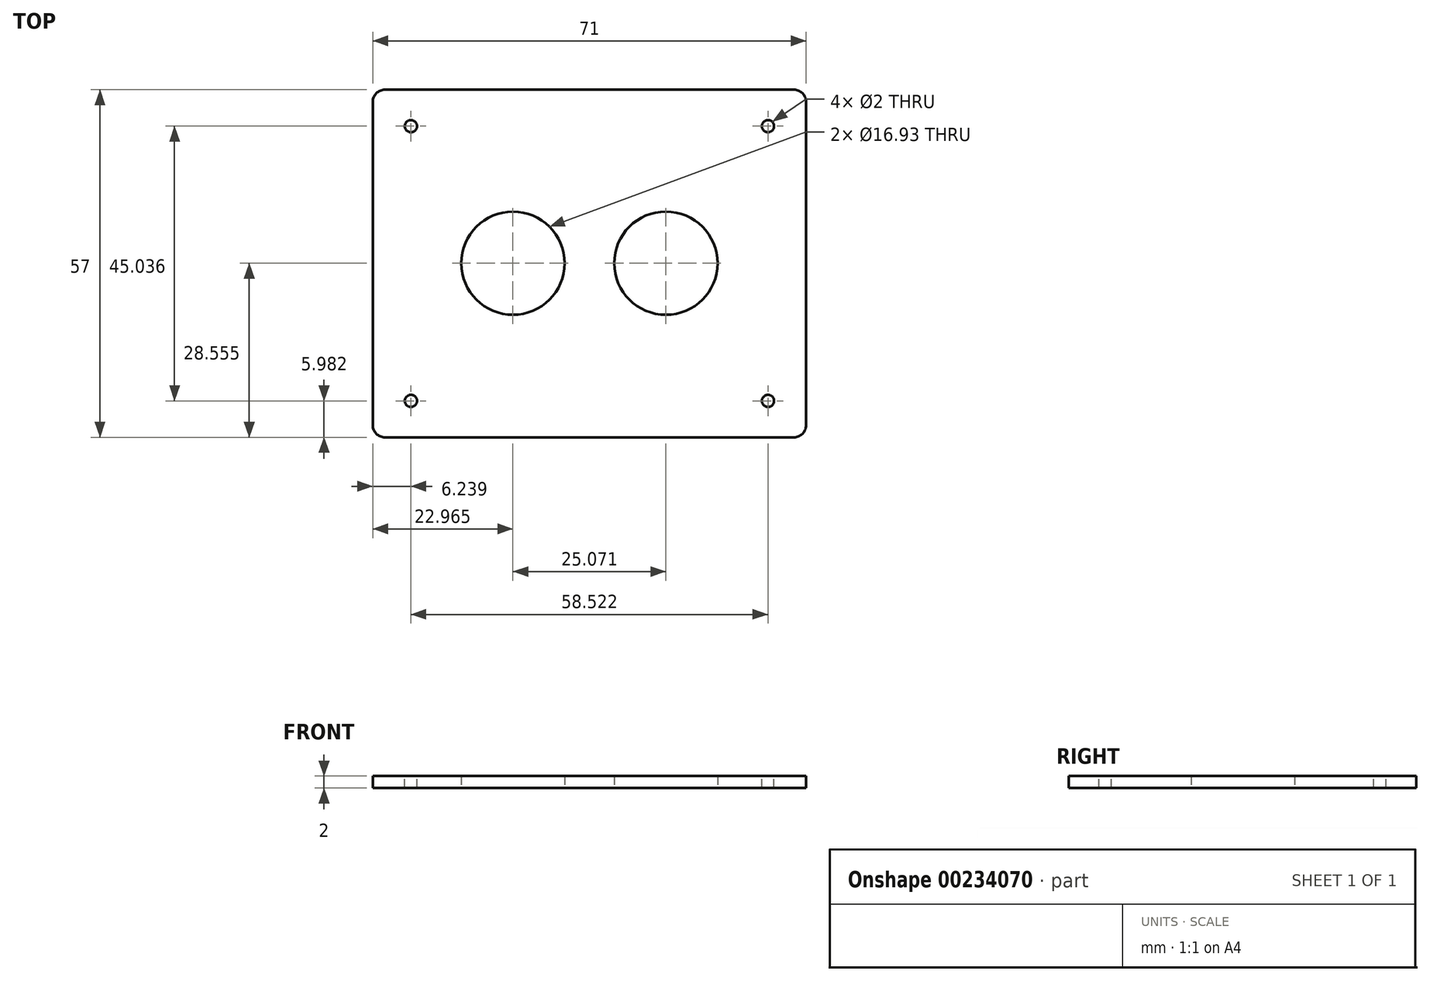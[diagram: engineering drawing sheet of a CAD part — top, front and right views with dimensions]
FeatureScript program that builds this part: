
annotation { "Feature Type Name" : "Feature", "Feature Type Description" : "" }
export const myFeature = defineFeature(function(context is Context, id is Id, definition is map)
    precondition{}
    {
        {
            var Q0;
            Q0=qCreatedBy(makeId("Top.planeOp"),FACE);
            var sketch = newSketch(context, id + "F0", { "sketchPlane" : qUnion([Q0])});
            skLineSegment(sketch, "E0.bottom", {"start": v(21, -8.5) * mm, "end": v(-21, -8.5) * mm, "construction": true});
            skLineSegment(sketch, "E0.top", {"start": v(21, 8.5) * mm, "end": v(-21, 8.5) * mm, "construction": true});
            skLineSegment(sketch, "E0.left", {"start": v(21, -8.5) * mm, "end": v(21, 8.5) * mm, "construction": true});
            skLineSegment(sketch, "E0.right", {"start": v(-21, -8.5) * mm, "end": v(-21, 8.5) * mm, "construction": true});
            skPoint(sketch, "E0.middle", {"position": v(0, 0) * mm});
            skLineSegment(sketch, "E1.bottom", {"start": v(35.5, -28.5) * mm, "end": v(-35.5, -28.5) * mm});
            skLineSegment(sketch, "E1.top", {"start": v(35.5, 28.5) * mm, "end": v(-35.5, 28.5) * mm});
            skLineSegment(sketch, "E1.left", {"start": v(35.5, -28.5) * mm, "end": v(35.5, 28.5) * mm});
            skLineSegment(sketch, "E1.right", {"start": v(-35.5, -28.5) * mm, "end": v(-35.5, 28.5) * mm});
            skPoint(sketch, "E2", {"position": v(-29.77, 22.85) * mm});
            skPoint(sketch, "E3.MirrorP", {"position": v(29.77, 22.85) * mm});
            skPoint(sketch, "E4.MirrorP", {"position": v(-29.77, -22.85) * mm});
            skPoint(sketch, "E5.MirrorP", {"position": v(29.77, -22.85) * mm});
            skCircle(sketch, "E6", {"center": v(-12.54, 0.06) * mm, "radius": 8.46 * mm});
            skPoint(sketch, "E6.first.point", {"position": v(-21, 0) * mm});
            skPoint(sketch, "E6.second.point", {"position": v(-4.07, 0) * mm});
            skPoint(sketch, "E6.second.point.positionSnap0", {"position": v(-21, 0) * mm});
            skPoint(sketch, "E6.third.point", {"position": v(-11.96, 8.5) * mm});
            skPoint(sketch, "E7.MirrorP", {"position": v(4.07, 0) * mm});
            skCircle(sketch, "E8.MirrorC", {"center": v(12.54, 0.06) * mm, "radius": 8.46 * mm});
            skSolve(sketch);
        }
        {
            var Q0;
            Q0=makeQuery(id+"F0.imprint","IMPRINT",FACE,{"disambiguationData":[TD([[makeQuery(id+"F0.imprint","IMPRINT",EDGE,{"derivedFrom":sQuery(id+"F0.wireOp",EDGE,"E1.bottom")}),-1.0]])]});
            extrude(context, id + "F1", {"entities" : qUnion([Q0]), "depth" : 2 * mm});
        }
        {
            var Q0;
            Q0=makeQuery(id+"F1.opExtrude","SWEPT_EDGE",EDGE,{"disambiguationData":[OSD([sQuery(id+"F0.wireOp",EDGE,"E1.top"),sQuery(id+"F0.wireOp",EDGE,"E1.right")])]});
            var Q1;
            Q1=makeQuery(id+"F1.opExtrude","SWEPT_EDGE",EDGE,{"disambiguationData":[OSD([sQuery(id+"F0.wireOp",EDGE,"E1.top"),sQuery(id+"F0.wireOp",EDGE,"E1.left")])]});
            var Q2;
            Q2=makeQuery(id+"F1.opExtrude","SWEPT_EDGE",EDGE,{"disambiguationData":[OSD([sQuery(id+"F0.wireOp",EDGE,"E1.bottom"),sQuery(id+"F0.wireOp",EDGE,"E1.left")])]});
            var Q3;
            Q3=makeQuery(id+"F1.opExtrude","SWEPT_EDGE",EDGE,{"disambiguationData":[OSD([sQuery(id+"F0.wireOp",EDGE,"E1.bottom"),sQuery(id+"F0.wireOp",EDGE,"E1.right")])]});
            fillet(context, id + "F2", {"entities" : qUnion([Q0, Q1, Q2, Q3]), "radius" : 2 * mm, "tangentPropagation" : true, "allowEdgeOverflow" : false});
        }
        {
            var Q0;
            Q0=makeQuery(id+"F1.opExtrude","CAP_FACE",FACE,{"disambiguationData":[OSD([sQuery(id+"F0.wireOp",EDGE,"E1.bottom"),sQuery(id+"F0.wireOp",EDGE,"E1.top"),sQuery(id+"F0.wireOp",EDGE,"E1.left"),sQuery(id+"F0.wireOp",EDGE,"E1.right"),sQuery(id+"F0.wireOp",EDGE,"E6"),sQuery(id+"F0.wireOp",EDGE,"E8.MirrorC")])],"isStart":false});
            var sketch = newSketch(context, id + "F3", { "sketchPlane" : qUnion([Q0])});
            skPoint(sketch, "E9", {"position": v(-29.26, 22.52) * mm});
            skPoint(sketch, "E10.MirrorP", {"position": v(29.26, 22.52) * mm});
            skPoint(sketch, "E11.MirrorP", {"position": v(-29.26, -22.52) * mm});
            skPoint(sketch, "E12.MirrorP", {"position": v(29.26, -22.52) * mm});
            skSolve(sketch);
        }
        {
            var Q0;
            Q0=sQuery(id+"F3.wireOp",VERTEX,"E9");
            var Q1;
            Q1=sQuery(id+"F3.wireOp",VERTEX,"E10.MirrorP");
            var Q2;
            Q2=sQuery(id+"F3.wireOp",VERTEX,"E11.MirrorP");
            var Q3;
            Q3=sQuery(id+"F3.wireOp",VERTEX,"E12.MirrorP");
            var Q4;
            Q4=makeQuery(id+"F1.opExtrude","SWEPT_BODY",BODY,{"disambiguationData":[OSD([sQuery(id+"F0.wireOp",EDGE,"E1.bottom"),sQuery(id+"F0.wireOp",EDGE,"E1.top"),sQuery(id+"F0.wireOp",EDGE,"E1.left"),sQuery(id+"F0.wireOp",EDGE,"E1.right"),sQuery(id+"F0.wireOp",EDGE,"E6"),sQuery(id+"F0.wireOp",EDGE,"E8.MirrorC")])]});
            hole(context, id + "F4", {"style" : HoleStyle.SIMPLE, "endStyle" : HoleEndStyle.THROUGH, "holeDiameter" : 2 * mm, "locations" : qUnion([Q0, Q1, Q2, Q3]), "scope" : qUnion([Q4]), "isTappedThrough" : true});
        }
    });
